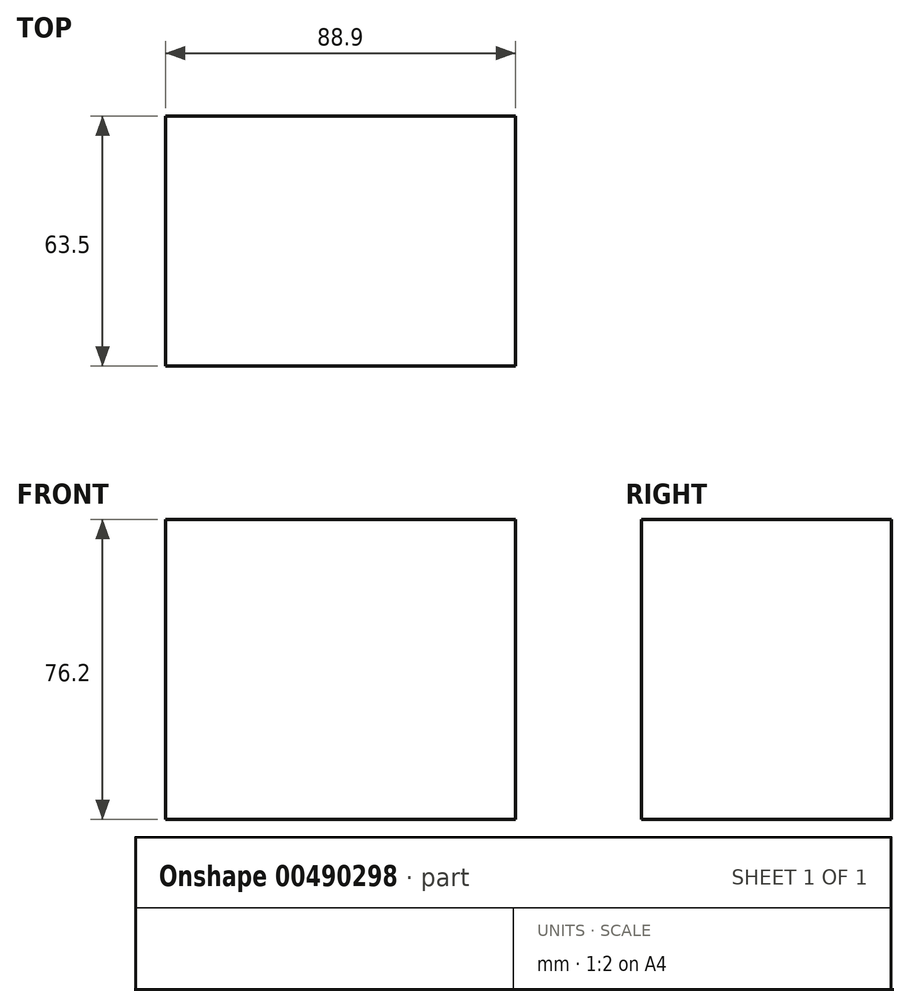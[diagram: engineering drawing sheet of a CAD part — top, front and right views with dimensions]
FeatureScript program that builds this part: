
annotation { "Feature Type Name" : "Feature", "Feature Type Description" : "" }
export const myFeature = defineFeature(function(context is Context, id is Id, definition is map)
    precondition{}
    {
        {
            var Q0;
            Q0=qCreatedBy(makeId("Top.planeOp"),FACE);
            var sketch = newSketch(context, id + "F0", { "sketchPlane" : qUnion([Q0])});
            skLineSegment(sketch, "E0.bottom", {"start": v(44.45, -31.75) * mm, "end": v(-44.45, -31.75) * mm});
            skLineSegment(sketch, "E0.top", {"start": v(44.45, 31.75) * mm, "end": v(-44.45, 31.75) * mm});
            skLineSegment(sketch, "E0.left", {"start": v(44.45, -31.75) * mm, "end": v(44.45, 31.75) * mm});
            skLineSegment(sketch, "E0.right", {"start": v(-44.45, -31.75) * mm, "end": v(-44.45, 31.75) * mm});
            skPoint(sketch, "E0.middle", {"position": v(0, 0) * mm});
            skSolve(sketch);
        }
        {
            var Q0;
            Q0 = qSketchRegion(id + "F0", true);
            extrude(context, id + "F1", {"entities" : qUnion([Q0]), "depth" : 76.2 * mm, "offsetDistance" : 25 * mm});
        }
    });
